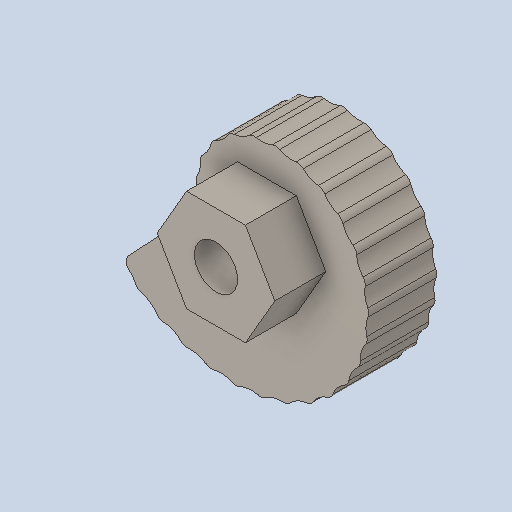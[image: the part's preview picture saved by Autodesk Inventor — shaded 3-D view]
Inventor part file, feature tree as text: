
AUTODESK INVENTOR PART (.ipt)
format: ipt  version: 2022.3 (Build 263350000, 350)  size: 198,656 bytes
history: native  units: in
note: dims shown in document units (in); Inventor stores cm internally (conversion verified against a paired STEP export)
features: fillet x1
ambient origin geometry x8: Origin, YZ Plane, XZ Plane, XY Plane, X Axis, Y Axis, Z Axis, Center Point
bodies: Solid1 (feature_tree)
feature tree (1):
  fillet  "Fillet1"  [1 undecoded]
note: 1 required parameter value undecoded (feature->parameter linkage not recoverable at this tier; creation-order binding heuristic only, values carry confidence <= 0.55)
